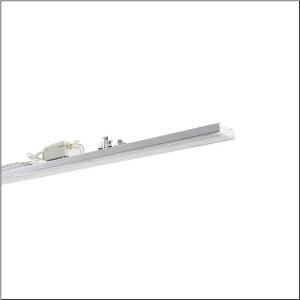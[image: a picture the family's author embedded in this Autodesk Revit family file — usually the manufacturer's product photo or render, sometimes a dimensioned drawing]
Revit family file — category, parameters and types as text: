
# Revit family: licross_r__21_recessed_mo_52tl12cn475g_df1a
name_source: partatom
category: Lighting Fixtures
units: mm (PartAtom-declared; Revit-internal decimal feet)

## family parameters
Cut with Voids When Loaded = No
Host = Face
Light Source = No
Part Type = Normal
Room Calculation Point = No
Round Connector Dimension = Use Diameter
Shared = No

## types (1)
- --- (1 x LED, 7990 lm, 42.6 W, 4000K)
    Apparent Load = 43 VA
    CIE Flux Codes = 72 92 99 100 100
    Color Rendering = 80
    Color Temperature = 4000K
    Default Elevation = 1800 mm
    Description = Licross® 21 Recessed MO, luminaire insert, of sheet steel, galvanised, coil coated, white, length: 1.500mm, width: 66mm, height: 67mm, LED rated luminous flux: 7.990lm, light colour: 840, control gear: ON/OFF Multilumen, CLOi, control gear: ECG Multilumen, with plug, 3-pole, with phase selection, mains connection: 220..240V, AC, 50/60Hz, halogen-free wiring, primary optical cover: cover, of PMMA, light emission: direct distribution, primary light characteristic: symmetric, protection rating (complete): IP40, insulation class (complete): insulation class I (protective earthing), certification: CE, ENEC, VDE, UKCA, protection symbol: D if used in an environment without relevant dust loads with corresponding accessories, impact resistance: IK06, permissible ambient temperature for indoor applications: -35..+45°C, corresponds to IFS (International Featured Standards) requirements for safety and quality in the food industry, reducing of maximum allowable ambient temperature of 5°C with ceiling mounting, LABS conformity tested according to VDMA 24364:2018-05, packaging unit: 1 piece
    Height = 58 mm
    Lamp = 1 x LED
    Lamp Light Flux = 7990 lm
    Lamp Power = 42.6 W
    Lamp count = 1
    Length = 1500 mm
    Luminous efficacy = 188 lm/W
    Manufacturer = Siteco
    ModVariant = No
    Model = 52TL12CN475G
    Mounting Place = Ceiling
    Mounting Type = Pendant
    Number of Poles = 1
    OnlyDefault = Yes
    Power Factor = 1
    Product Name = Licross® 21 Recessed MO
    Product group = luminaire insert
    ProductGroupID = 901
    Protection Class = Protection class I
    Protection Degree = IP 40
    RLX_Detail_Level = 1
    RLX_Emergency_Light_Flux = 0 lm
    RLX_Emergency_Type = 0
    RLX_Emergency_Type_DB = No
    RlxData = <blob elided: 22341 chars, md5=e4dc05f7>
    Socket = socket
    Standby Power = 0 W
    System Light Flux = 7990 lm
    System Power = 43 W
    Type Comments = factory setting: luminous flux: 100 % | (A | C | E) | 99 mA
    Type Image = l_1296930.jpg
    URL = http://relux.com
    VarID = @adj_040721
    Voltage = 0 V
    Weight = 0.00 kg
    Width = 66 mm

## geometry (parser evidence)
native form markers: Blend x4, Sweep x10
no freeform markers — native parametric forms only
